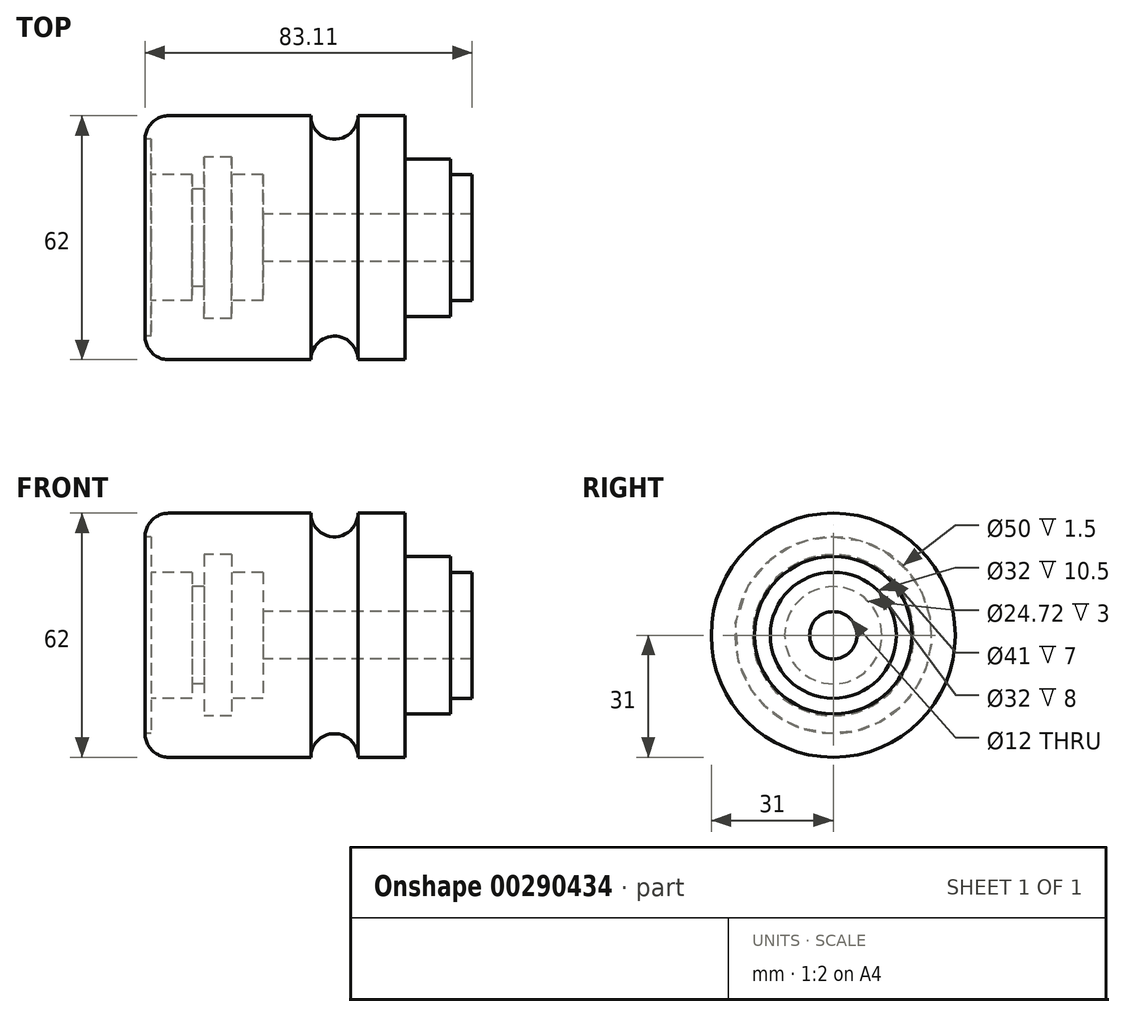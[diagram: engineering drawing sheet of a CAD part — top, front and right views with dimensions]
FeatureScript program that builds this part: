
annotation { "Feature Type Name" : "Feature", "Feature Type Description" : "" }
export const myFeature = defineFeature(function(context is Context, id is Id, definition is map)
    precondition{}
    {
        {
            var Q0;
            Q0=qCreatedBy(makeId("Front.planeOp"),FACE);
            var sketch = newSketch(context, id + "F0", { "sketchPlane" : qUnion([Q0])});
            skLineSegment(sketch, "E0", {"start": v(-54.93, 0) * mm, "end": v(55.3, 0) * mm, "construction": true});
            skLineSegment(sketch, "E1", {"start": v(-49.14, 31) * mm, "end": v(-13.04, 31) * mm});
            skArc(sketch, "E2", {"start": v(-13.04, 31) * mm, "mid": v(-7.04, 25) * mm, "end": v(-1.04, 31) * mm});
            skLineSegment(sketch, "E3", {"start": v(-1.04, 31) * mm, "end": v(10.96, 31) * mm});
            skLineSegment(sketch, "E4", {"start": v(27.97, 16) * mm, "end": v(27.97, 6) * mm});
            skLineSegment(sketch, "E5", {"start": v(27.97, 6) * mm, "end": v(-25.14, 6) * mm});
            skLineSegment(sketch, "E6", {"start": v(-55.14, 25) * mm, "end": v(-53.64, 25) * mm});
            skLineSegment(sketch, "E7", {"start": v(-53.64, 25) * mm, "end": v(-53.64, 16) * mm});
            skLineSegment(sketch, "E8", {"start": v(-53.64, 16) * mm, "end": v(-43.14, 16) * mm});
            skLineSegment(sketch, "E9", {"start": v(-43.14, 16) * mm, "end": v(-43.14, 12.36) * mm});
            skLineSegment(sketch, "E10", {"start": v(-43.14, 12.36) * mm, "end": v(-40.14, 12.36) * mm});
            skLineSegment(sketch, "E11", {"start": v(-40.14, 12.36) * mm, "end": v(-40.14, 20.5) * mm});
            skLineSegment(sketch, "E12", {"start": v(-40.14, 20.5) * mm, "end": v(-33.14, 20.5) * mm});
            skLineSegment(sketch, "E13", {"start": v(-33.14, 20.5) * mm, "end": v(-33.14, 16) * mm});
            skLineSegment(sketch, "E14", {"start": v(-33.14, 16) * mm, "end": v(-25.14, 16) * mm});
            skLineSegment(sketch, "E15", {"start": v(-25.14, 16) * mm, "end": v(-25.14, 6) * mm});
            skArc(sketch, "E16", {"start": v(-55.14, 25) * mm, "mid": v(-53.38, 29.24) * mm, "end": v(-49.14, 31) * mm});
            skLineSegment(sketch, "E17", {"start": v(10.96, 31) * mm, "end": v(10.96, 20) * mm});
            skLineSegment(sketch, "E18", {"start": v(10.96, 20) * mm, "end": v(22.5, 20) * mm});
            skLineSegment(sketch, "E19", {"start": v(22.5, 20) * mm, "end": v(22.5, 16) * mm});
            skLineSegment(sketch, "E20", {"start": v(22.5, 16) * mm, "end": v(27.97, 16) * mm});
            skSolve(sketch);
        }
        {
            var Q0;
            Q0=makeQuery(id+"F0.imprint","IMPRINT",FACE,{"disambiguationData":[TD([[makeQuery(id+"F0.imprint","IMPRINT",EDGE,{"derivedFrom":sQuery(id+"F0.wireOp",EDGE,"E1")}),-1.0]])]});
            var Q1;
            Q1=sQuery(id+"F0.wireOp",EDGE,"E0");
            revolve(context, id + "F1", {"entities" : qUnion([Q0]), "axis" : qUnion([Q1]), "revolveType" : RevolveType.FULL});
        }
    });
